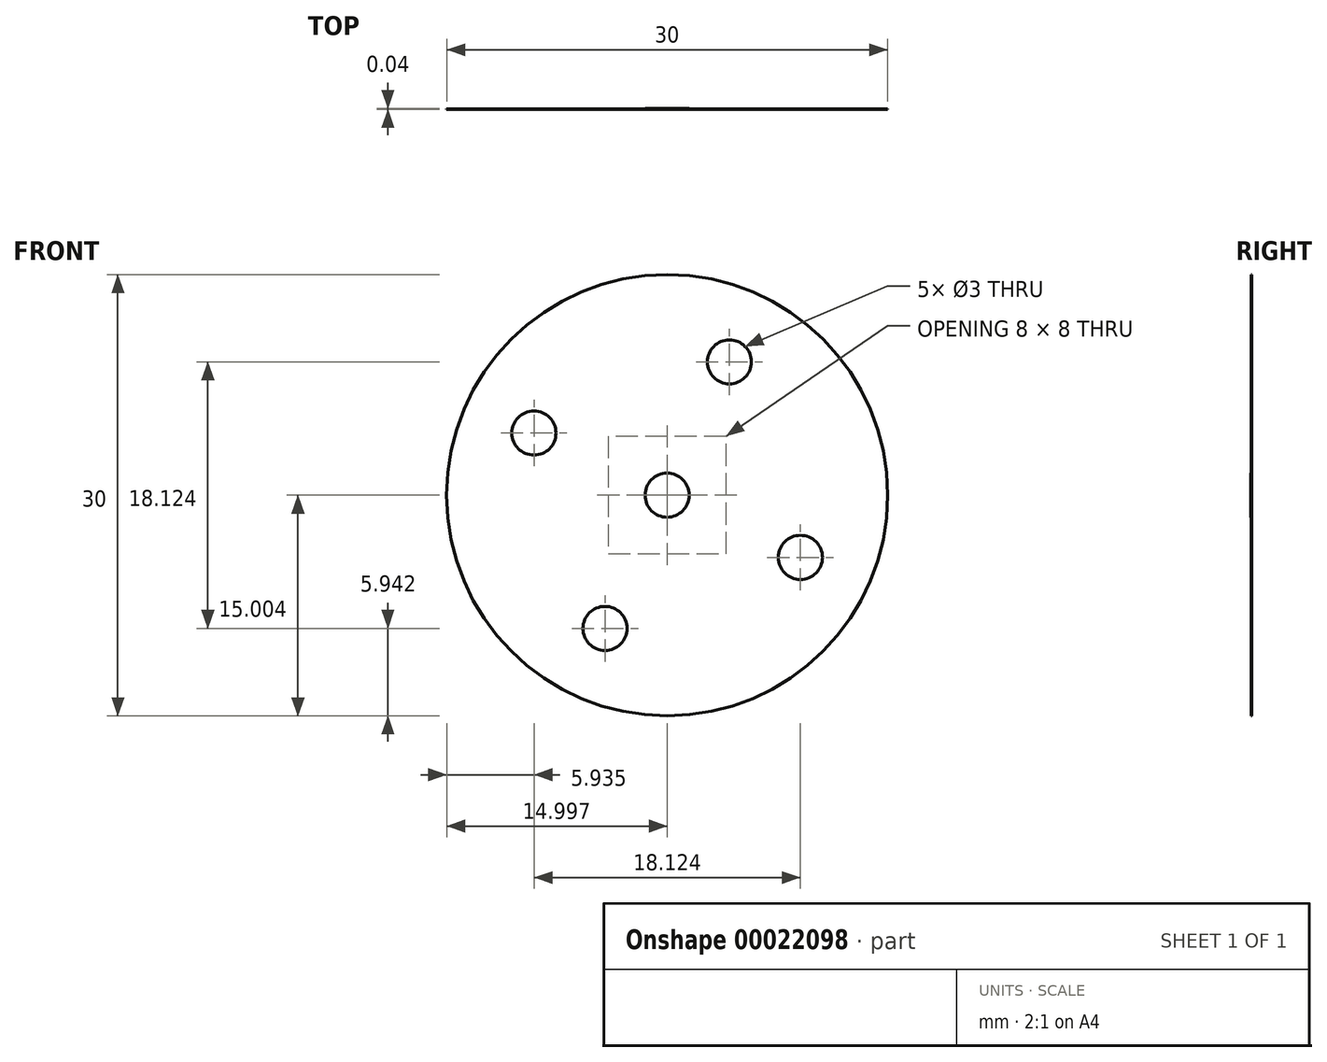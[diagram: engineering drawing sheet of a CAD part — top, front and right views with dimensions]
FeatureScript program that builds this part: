
annotation { "Feature Type Name" : "Feature", "Feature Type Description" : "" }
export const myFeature = defineFeature(function(context is Context, id is Id, definition is map)
    precondition{}
    {
        {
            var Q0;
            Q0=qCreatedBy(makeId("Front.planeOp"),FACE);
            var sketch = newSketch(context, id + "F0", { "sketchPlane" : qUnion([Q0])});
            skCircle(sketch, "E0", {"center": v(13.4, 32.62) * mm, "radius": 15 * mm});
            skCircle(sketch, "E1", {"center": v(13.4, 32.62) * mm, "radius": 1.5 * mm});
            skCircle(sketch, "E2", {"center": v(13.4, 32.62) * mm, "radius": 4 * mm});
            skCircle(sketch, "E3", {"center": v(4.34, 36.85) * mm, "radius": 1.5 * mm});
            skCircle(sketch, "E4.1.0", {"center": v(9.17, 23.56) * mm, "radius": 1.5 * mm});
            skCircle(sketch, "E4.2.0", {"center": v(22.46, 28.4) * mm, "radius": 1.5 * mm});
            skCircle(sketch, "E4.3.0", {"center": v(17.63, 41.69) * mm, "radius": 1.5 * mm});
            skSolve(sketch);
        }
        {
            var Q0;
            Q0=makeQuery(id+"F0.imprint","IMPRINT",FACE,{"disambiguationData":[TD([[makeQuery(id+"F0.imprint","IMPRINT",EDGE,{"derivedFrom":sQuery(id+"F0.wireOp",EDGE,"E1")}),-1.0]])]});
            extrude(context, id + "F1", {"entities" : qUnion([Q0]), "endBound" : BoundingType.SYMMETRIC, "depth" : 4 / 100 * mm});
        }
        {
            var Q0;
            Q0=makeQuery(id+"F0.imprint","IMPRINT",FACE,{"disambiguationData":[TD([[makeQuery(id+"F0.imprint","IMPRINT",EDGE,{"derivedFrom":sQuery(id+"F0.wireOp",EDGE,"E0")}),1.0]])]});
            extrude(context, id + "F2", {"entities" : qUnion([Q0]), "operationType" : NewBodyOperationType.ADD, "endBound" : BoundingType.SYMMETRIC, "depth" : 3 / 100 * mm});
        }
    });
